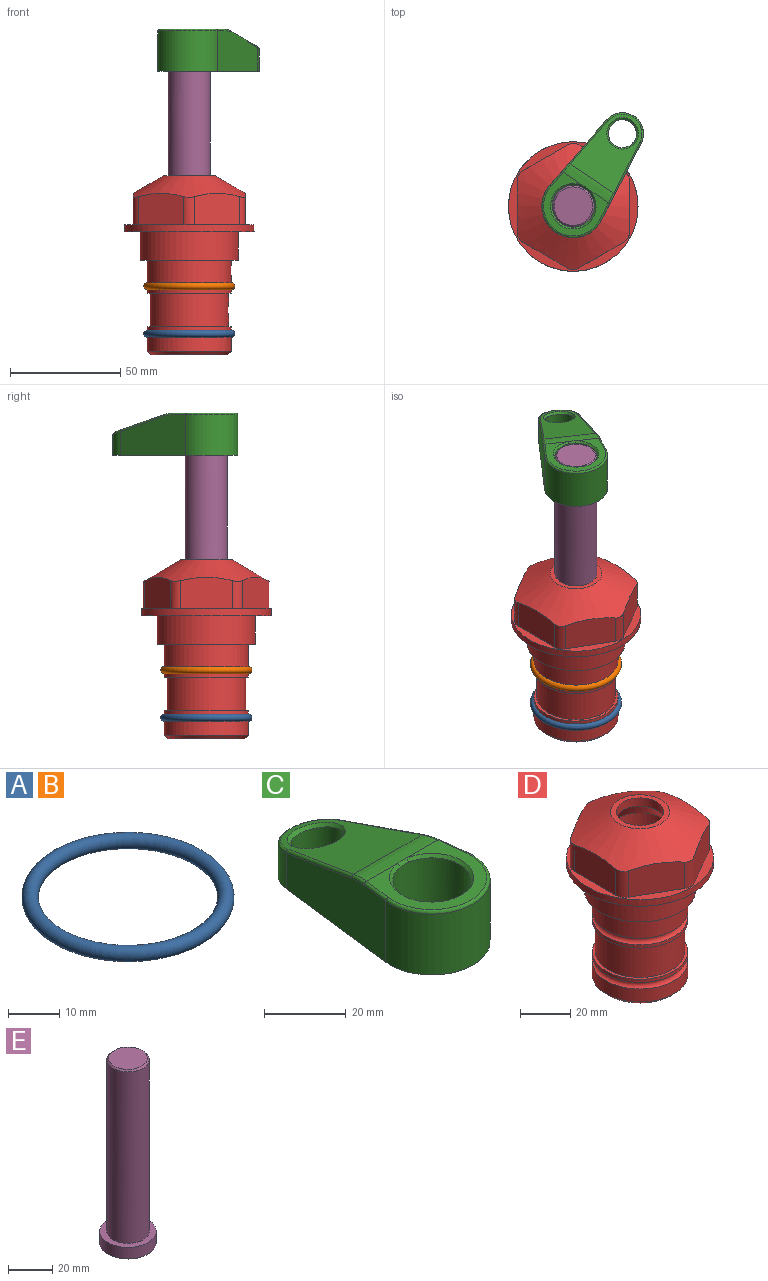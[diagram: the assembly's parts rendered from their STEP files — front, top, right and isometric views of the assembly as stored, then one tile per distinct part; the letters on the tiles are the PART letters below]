
ASSEMBLY  parts=5 mates=4
PART A: 1 faces, bbox 44.7x44.7x3.2 mm
  f0: torus R=19.05mm, axis (0,0,1), area 1193.9mm2
PART B: same geometry as A
PART C: 31 faces, bbox 31.7x65.5x19.8 mm
  f0: plane 39.12x18.26mm, normal (0.99,0.12,0), area 612.2mm2, adj f1,f4,f7,f11,f13,f15
  f1: cylinder r=9.53mm len=18.91mm, axis (0,0,-1), area 296.1mm2, adj f0,f2,f7,f17
  f2: plane 39.12x18.26mm, normal (-0.99,0.12,0), area 612.2mm2, adj f1,f4,f7,f12,f14,f16
  f3: cylinder r=6.35mm len=12.7mm, axis (0,0,-1), area 362.4mm2, adj f7,f18
  f4: cylinder r=14.29mm len=28.58mm, axis (0,0,-1), area 882.2mm2, adj f0,f2,f7,f10
  f5: cylinder r=9.53mm len=19.05mm, axis (0,0,-1), area 1092.6mm2, adj f7,f19,f20
  f6: plane 26.99x23.69mm, normal (0,0,1), area 216.2mm2, adj f9,f10,f11,f12,f19
  f7: plane 63.5x28.58mm, normal (0,0,-1), area 661.8mm2, adj f0,f1,f2,f3,f4,f5,f22,f23
  f8: plane 33.52x23.6mm, normal (0,0.26,0.97), area 486mm2, adj f9,f15,f16,f17,f18
  f9: cylinder r=19.05mm len=24.72mm, axis (1,0,0), area 120.4mm2, adj f6,f8,f13,f14,f20
  f10: torus R=13.49mm, axis (0,0,1), area 59mm2, adj f4,f6,f11,f12
  f11: cylinder r=0.79mm len=8.67mm, axis (0.12,-0.99,0), area 10.8mm2, adj f0,f6,f10,f13
  f12: cylinder r=0.79mm len=8.67mm, axis (0.12,0.99,0), area 10.8mm2, adj f2,f6,f10,f14
  f13: bspline ~4.95x1.42mm, area 6.1mm2, adj f0,f9,f11,f15
  f14: bspline ~4.95x1.42mm, area 6.1mm2, adj f2,f9,f12,f16
  f15: cylinder r=0.79mm len=25.95mm, axis (0.12,-0.96,0.26), area 32.9mm2, adj f0,f8,f13,f17
  f16: cylinder r=0.79mm len=25.95mm, axis (0.12,0.96,-0.26), area 32.9mm2, adj f2,f8,f14,f17
  f17: bspline ~18.91x8.38mm, area 30mm2, adj f1,f8,f15,f16
  f18: bspline ~14.29x14.29mm, area 48.3mm2, adj f3,f8
  f19: cone r=9.53mm half-angle=45deg, axis (0,0,1), area 66.5mm2, adj f5,f6,f20
  f20: bspline ~3.22x0.96mm, area 3.5mm2, adj f5,f9,f19
  f21: plane 2.75x2.72mm, normal (0,0,-1), area 2.9mm2, adj f23,f25,f28
  f22: plane 23.05x15.88mm, normal (-0.99,-0.12,0), area 323.6mm2, adj f7,f25,f26,f27,f28,f29
  f23: plane 23.05x15.88mm, normal (0.99,-0.12,0), area 323.6mm2, adj f7,f21,f25,f27,f28,f30
  f24: cylinder r=9.53mm len=10.69mm, axis (0,0,-1), area 114.7mm2, adj f7,f27,f29,f30
  f25: cylinder r=12.7mm len=20.59mm, axis (0,0,-1), area 381.1mm2, adj f7,f21,f22,f23,f26,f28
  f26: plane 2.75x2.72mm, normal (0,0,-1), area 2.9mm2, adj f22,f25,f28
  f27: plane 19.72x18.37mm, normal (0,-0.26,-0.97), area 291.8mm2, adj f22,f23,f24,f28,f29,f30
  f28: cylinder r=15.88mm len=19.92mm, axis (1,0,0), area 54.8mm2, adj f21,f22,f23,f25,f26,f27
  f29: cylinder r=1.59mm len=11mm, axis (0,0,-1), area 34.7mm2, adj f7,f22,f24,f27
  f30: cylinder r=1.59mm len=11mm, axis (0,0,-1), area 34.7mm2, adj f7,f23,f24,f27
PART D: 36 faces, bbox 58.7x58.7x81 mm
  f0: cylinder r=17.78mm len=35.56mm, axis (0,0,1), area 1670.8mm2, adj f23,f24,f31
  f1: cylinder r=19.05mm len=38.1mm, axis (0,0,1), area 1191.9mm2, adj f26,f27,f30
  f2: plane 58.66x58.66mm, normal (0,0,-1), area 1150.6mm2, adj f3,f28
  f3: cylinder r=29.33mm len=58.66mm, axis (0,0,-1), area 585.1mm2, adj f2,f4
  f4: plane 58.66x58.66mm, normal (0,0,1), area 475.9mm2, adj f3,f5,f6,f7,f8,f9,f10,f11
  f5: plane 20.32x14.34mm, normal (-0.5,0.87,0), area 324.4mm2, adj f4,f15,f16,f17
  f6: plane 20.32x14.34mm, normal (0.5,0.87,0), area 324.4mm2, adj f4,f14,f15,f17
  f7: plane 23.48x14.34mm, normal (1,0,0), area 324.4mm2, adj f4,f13,f14,f17
  f8: plane 20.32x14.34mm, normal (0.5,-0.87,0), area 324.4mm2, adj f4,f12,f13,f17
  f9: plane 20.32x14.34mm, normal (-0.5,-0.87,0), area 324.4mm2, adj f4,f11,f12,f17
  f10: plane 23.48x14.34mm, normal (-1,0,0), area 324.4mm2, adj f4,f11,f16,f17
  f11: cylinder r=5.08mm len=12.85mm, axis (0,0,-1), area 67.2mm2, adj f4,f9,f10,f17
  f12: cylinder r=5.08mm len=12.85mm, axis (0,0,-1), area 67.2mm2, adj f4,f8,f9,f17
  f13: cylinder r=5.08mm len=12.85mm, axis (0,0,-1), area 67.2mm2, adj f4,f7,f8,f17
  f14: cylinder r=5.08mm len=12.85mm, axis (0,0,-1), area 67.2mm2, adj f4,f6,f7,f17
  f15: cylinder r=5.08mm len=12.85mm, axis (0,0,-1), area 67.2mm2, adj f4,f5,f6,f17
  f16: cylinder r=5.08mm len=12.85mm, axis (0,0,-1), area 67.2mm2, adj f4,f5,f10,f17
  f17: cone r=11.73mm half-angle=60deg, axis (0,0,-1), area 2071.8mm2, adj f5,f6,f7,f8,f9,f10,f11,f12
  f18: plane 23.46x23.46mm, normal (0,0,1), area 147.4mm2, adj f17,f35
  f19: plane 34.93x34.93mm, normal (0,0,-1), area 958mm2, adj f29
  f20: cylinder r=19.05mm len=38.1mm, axis (0,0,1), area 760.1mm2, adj f21,f29
  f21: torus R=19.05mm, axis (0,0,1), area 565.3mm2, adj f20,f22
  f22: cylinder r=19.05mm len=38.1mm, axis (0,0,1), area 190mm2, adj f21,f23
  f23: plane 38.1x38.1mm, normal (0,0,1), area 146.9mm2, adj f0,f22
  f24: plane 38.1x38.1mm, normal (0,0,-1), area 146.9mm2, adj f0,f25
  f25: cylinder r=19.05mm len=38.1mm, axis (0,0,1), area 190mm2, adj f24,f26
  f26: torus R=19.05mm, axis (0,0,1), area 565.3mm2, adj f1,f25
  f27: plane 44.45x44.45mm, normal (0,0,-1), area 411.7mm2, adj f1,f28
  f28: cylinder r=22.23mm len=44.45mm, axis (0,0,1), area 1773.5mm2, adj f2,f27
  f29: cone r=19.05mm half-angle=45deg, axis (0,0,1), area 257.5mm2, adj f19,f20
  f30: cylinder r=3.17mm len=6.75mm, axis (-1,0,0), area 128mm2, adj f1,f33
  f31: cylinder r=3.17mm len=6.35mm, axis (-1,0,0), area 102.5mm2, adj f0,f33
  f32: plane 25.4x25.4mm, normal (0,0,1), area 506.7mm2, adj f33
  f33: cylinder r=12.7mm len=66.42mm, axis (0,0,-1), area 5236.2mm2, adj f30,f31,f32,f34
  f34: cone r=9.53mm half-angle=30deg, axis (0,0,-1), area 443.4mm2, adj f33,f35
  f35: cylinder r=9.53mm len=19.05mm, axis (0,0,-1), area 240.9mm2, adj f18,f34
PART E: 6 faces, bbox 25.4x25.4x101.6 mm
  f0: plane 17.46x17.46mm, normal (0,0,1), area 239.5mm2, adj f5
  f1: plane 25.4x25.4mm, normal (0,0,-1), area 506.7mm2, adj f2
  f2: cylinder r=12.7mm len=25.4mm, axis (0,0,1), area 506.7mm2, adj f1,f3
  f3: plane 25.4x25.4mm, normal (0,0,1), area 221.7mm2, adj f2,f4
  f4: cylinder r=9.53mm len=94.46mm, axis (0,0,1), area 5653mm2, adj f3,f5
  f5: cone r=8.73mm half-angle=45deg, axis (0,0,-1), area 64.4mm2, adj f0,f4
PLACE A t=(0,0,-21.59)mm
PLACE B at identity
PLACE C rot(axis=(0,0,-1),34.1deg) t=(0,0,28.35)mm
PLACE D at identity fixed
PLACE E rot(axis=(0,0,-1),34.1deg) t=(0,0,27.55)mm
MATE cylindrical D.f0 <-> E.f2  axis (0,0,1) through (0,0,-50.55)mm
MATE fastened A.f0 <-> D.f0  axis (0,0,1) through (0,0,-46.1)mm
MATE fastened B.f0 <-> D.f0  axis (0,0,1) through (0,0,-24.51)mm
MATE fastened C.f4 <-> E.f2  axis (0,0,-1) through (0,0,91.05)mm
